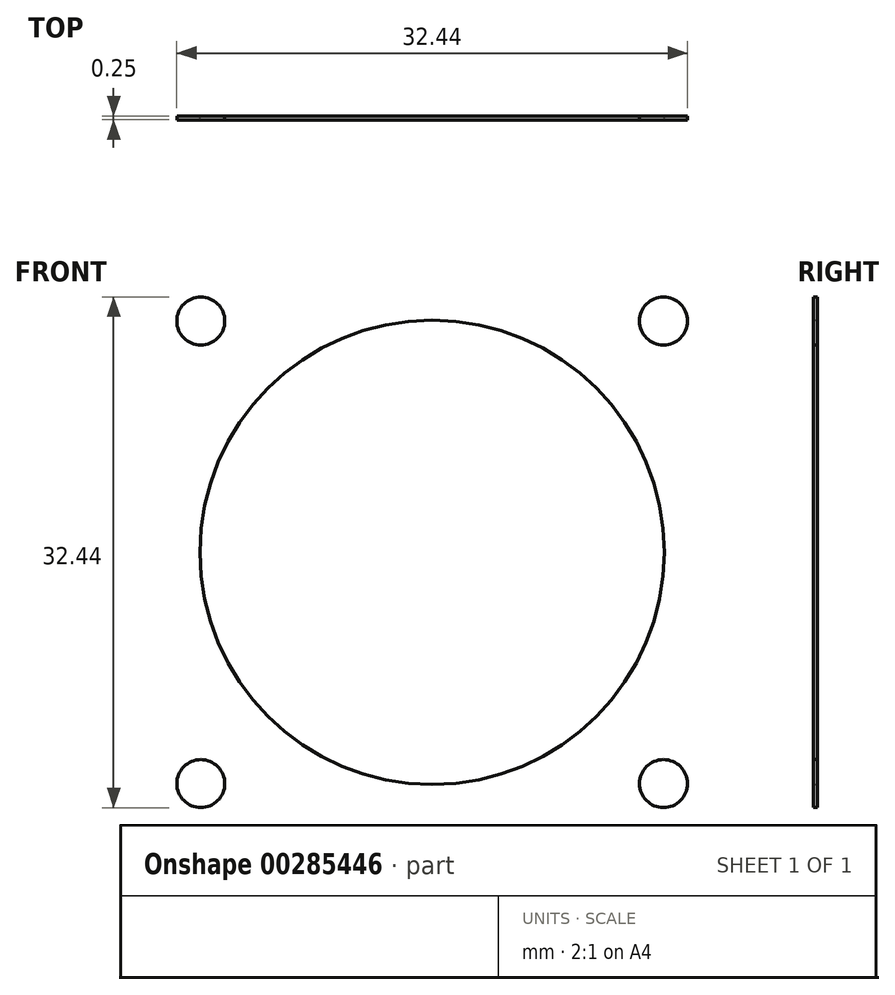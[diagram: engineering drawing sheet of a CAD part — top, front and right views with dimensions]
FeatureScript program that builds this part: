
annotation { "Feature Type Name" : "Feature", "Feature Type Description" : "" }
export const myFeature = defineFeature(function(context is Context, id is Id, definition is map)
    precondition{}
    {
        {
            var Q0;
            Q0=qCreatedBy(makeId("Front.planeOp"),FACE);
            var sketch = newSketch(context, id + "F0", { "sketchPlane" : qUnion([Q0])});
            skCircle(sketch, "E0", {"center": v(0, 0) * mm, "radius": 14.74 * mm});
            skLineSegment(sketch, "E1.bottom", {"start": v(-14.7, 14.7) * mm, "end": v(14.7, 14.7) * mm, "construction": true});
            skLineSegment(sketch, "E1.top", {"start": v(-14.7, -14.7) * mm, "end": v(14.7, -14.7) * mm, "construction": true});
            skLineSegment(sketch, "E1.left", {"start": v(-14.7, 14.7) * mm, "end": v(-14.7, -14.7) * mm, "construction": true});
            skLineSegment(sketch, "E1.right", {"start": v(14.7, 14.7) * mm, "end": v(14.7, -14.7) * mm, "construction": true});
            skLineSegment(sketch, "E2", {"start": v(14.7, 0) * mm, "end": v(-14.7, 0) * mm, "construction": true});
            skLineSegment(sketch, "E3", {"start": v(0, -14.7) * mm, "end": v(0, 14.7) * mm, "construction": true});
            skCircle(sketch, "E4", {"center": v(-14.7, 14.7) * mm, "radius": 1.52 * mm});
            skCircle(sketch, "E5", {"center": v(14.7, 14.7) * mm, "radius": 1.52 * mm});
            skCircle(sketch, "E6", {"center": v(14.7, -14.7) * mm, "radius": 1.52 * mm});
            skCircle(sketch, "E7", {"center": v(-14.7, -14.7) * mm, "radius": 1.52 * mm});
            skSolve(sketch);
        }
        {
            var Q0;
            Q0=makeQuery(id+"F0.imprint","IMPRINT",FACE,{"disambiguationData":[TD([[makeQuery(id+"F0.imprint","IMPRINT",EDGE,{"derivedFrom":sQuery(id+"F0.wireOp",EDGE,"E0")}),1.0]])]});
            var Q1;
            Q1=makeQuery(id+"F0.imprint","IMPRINT",FACE,{"disambiguationData":[TD([[makeQuery(id+"F0.imprint","IMPRINT",EDGE,{"derivedFrom":sQuery(id+"F0.wireOp",EDGE,"E4")}),1.0]])]});
            var Q2;
            Q2=makeQuery(id+"F0.imprint","IMPRINT",FACE,{"disambiguationData":[TD([[makeQuery(id+"F0.imprint","IMPRINT",EDGE,{"derivedFrom":sQuery(id+"F0.wireOp",EDGE,"E5")}),1.0]])]});
            var Q3;
            Q3=makeQuery(id+"F0.imprint","IMPRINT",FACE,{"disambiguationData":[TD([[makeQuery(id+"F0.imprint","IMPRINT",EDGE,{"derivedFrom":sQuery(id+"F0.wireOp",EDGE,"E6")}),1.0]])]});
            var Q4;
            Q4=makeQuery(id+"F0.imprint","IMPRINT",FACE,{"disambiguationData":[TD([[makeQuery(id+"F0.imprint","IMPRINT",EDGE,{"derivedFrom":sQuery(id+"F0.wireOp",EDGE,"E7")}),1.0]])]});
            extrude(context, id + "F1", {"entities" : qUnion([Q0, Q1, Q2, Q3, Q4]), "depth" : 0.25 * mm});
        }
    });
